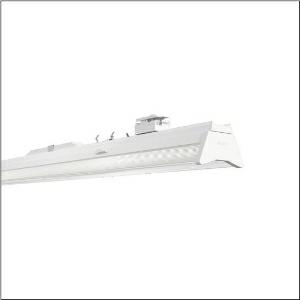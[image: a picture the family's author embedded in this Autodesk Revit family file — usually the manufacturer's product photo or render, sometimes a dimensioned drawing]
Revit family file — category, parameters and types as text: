
# Revit family: licross_11_performance_tw_51td16tnt85x
name_source: partatom
category: Lighting Fixtures
units: mm (PartAtom-declared; Revit-internal decimal feet)

## family parameters
Cut with Voids When Loaded = No
Host = Face
Light Source = No
Part Type = Normal
Room Calculation Point = No
Round Connector Dimension = Use Diameter
Shared = No

## types (1)
- --- (1 x LED 2700 K ... 6500 K, 8930 lm, 56 W, 2700K)
    Apparent Load = 56 VA
    CIE Flux Codes = 63 87 95 78 100
    Color Rendering = 80
    Color Temperature = 2700K
    Default Elevation = 1800 mm
    Description = Licross 11 Performance TW, luminaire insert, of sheet steel, galvanised, coil coated, white, length: 1.500mm, width: 120mm, height: 123mm, LED rated luminous flux: 8.930lm, light colour: 8tw, SDCM (Standard Deviation of Colour Matching)MacAdam ≤ 2 SDCM (initial), control gear: DALI DT8, with plug, 5-pole, with phase selection, mains connection: 220..240V, AC, 50/60Hz, rated input power: 56W, internal wiring halogen-free, primary light control with lens, of plastic, primary optical cover: cover, of PMMA, light emission: direct/indirect distribution, primary light characteristic: symmetric, protection rating (complete): IP54, insulation class (complete): insulation class I (protective earthing), certification: CE, ENEC, VDE, UKCA, protection symbol: D if used in an environment with non-conductive dust loads with corresponding accessories, impact resistance: IK06, permissible ambient temperature for indoor applications: -25..+35°C, corresponds to IFS (International Featured Standards) requirements for safety and quality in the food industry, reducing of maximum allowable ambient temperature of 5°C with ceiling mounting, LABS conformity tested according to VDMA 24364:2018-05, The light source and the operating device comply with the requirements of the Ecodesign Regulation (EU) 2019/2020 and are replaceable in accordance with this regulation, packaging unit: 1 piece
    Height = 114 mm
    Lamp = 1 x LED 2700 K ... 6500 K
    Lamp Light Flux = 8930 lm
    Lamp Power = 56 W
    Lamp count = 1
    Length = 1500 mm
    Luminous efficacy = 159 lm/W
    Manufacturer = Siteco
    ModVariant = No
    Model = 51TD16TNT85X
    Mounting Place = Ceiling
    Mounting Type = Pendant
    Number of Poles = 1
    OnlyDefault = Yes
    Power Factor = 1
    Product Name = Licross 11 Performance TW
    Product group = luminaire insert | ceiling pendant
    ProductGroupID = 901
    Protection Class = Protection class I
    Protection Degree = IP 54
    RLX_Detail_Level = 1
    RLX_Emergency_Light_Flux = 0 lm
    RLX_Emergency_Type = 0
    RLX_Emergency_Type_DB = No
    RlxData = <blob elided: 30709 chars, md5=2d2524c1>
    Socket = socket
    Standby Power = 0 W
    System Light Flux = 8930 lm
    System Power = 56 W
    Type Comments = individual setting: CCT=2700K
    Type Image = l_1256138.jpg
    URL = http://relux.com
    VarID = @adj_056363
    Voltage = 0 V
    Weight = 0.00 kg
    Width = 120 mm

## geometry (parser evidence)
native form markers: Blend x4, Sweep x10
no freeform markers — native parametric forms only
